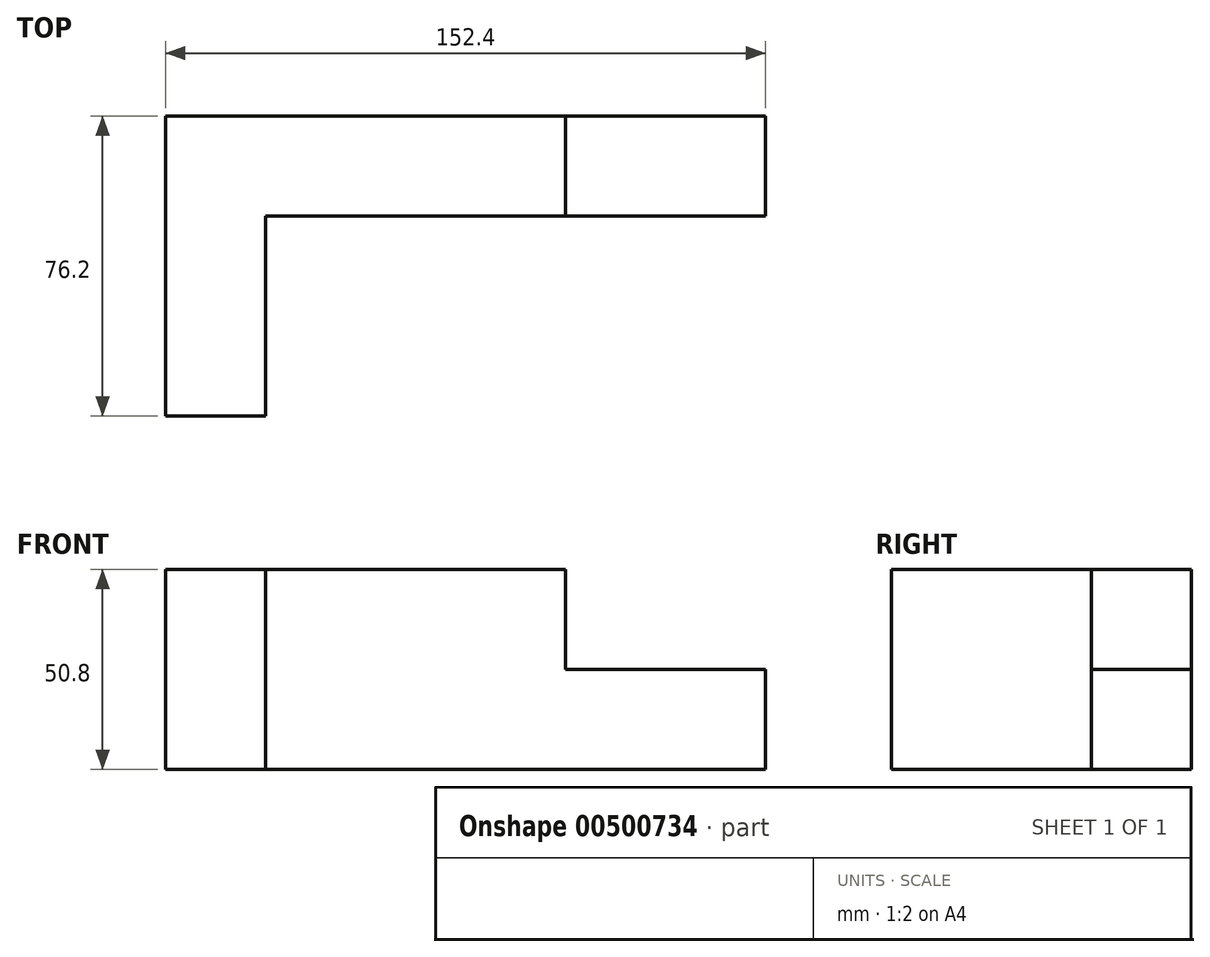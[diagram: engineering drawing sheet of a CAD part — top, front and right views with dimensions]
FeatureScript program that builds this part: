
annotation { "Feature Type Name" : "Feature", "Feature Type Description" : "" }
export const myFeature = defineFeature(function(context is Context, id is Id, definition is map)
    precondition{}
    {
        {
            var Q0;
            Q0=qCreatedBy(makeId("Top.planeOp"),FACE);
            var sketch = newSketch(context, id + "F0", { "sketchPlane" : qUnion([Q0])});
            skLineSegment(sketch, "E0.bottom", {"start": v(-48.05, 62.68) * mm, "end": v(-22.65, 62.68) * mm});
            skLineSegment(sketch, "E0.top", {"start": v(-48.05, -13.52) * mm, "end": v(-22.65, -13.52) * mm});
            skLineSegment(sketch, "E0.left", {"start": v(-48.05, 62.68) * mm, "end": v(-48.05, -13.52) * mm});
            skLineSegment(sketch, "E0.right", {"start": v(-22.65, 62.68) * mm, "end": v(-22.65, -13.52) * mm});
            skLineSegment(sketch, "E1.bottom", {"start": v(-22.65, 62.68) * mm, "end": v(53.55, 62.68) * mm});
            skLineSegment(sketch, "E1.top", {"start": v(-22.65, 37.28) * mm, "end": v(53.55, 37.28) * mm});
            skLineSegment(sketch, "E1.left", {"start": v(-22.65, 62.68) * mm, "end": v(-22.65, 37.28) * mm});
            skLineSegment(sketch, "E1.right", {"start": v(53.55, 62.68) * mm, "end": v(53.55, 37.28) * mm});
            skLineSegment(sketch, "E2.bottom", {"start": v(53.55, 62.68) * mm, "end": v(104.35, 62.68) * mm});
            skLineSegment(sketch, "E2.top", {"start": v(53.55, 37.28) * mm, "end": v(104.35, 37.28) * mm});
            skLineSegment(sketch, "E2.right", {"start": v(104.35, 62.68) * mm, "end": v(104.35, 37.28) * mm});
            skSolve(sketch);
        }
        {
            var Q0;
            Q0=makeQuery(id+"F0.imprint","IMPRINT",FACE,{"disambiguationData":[TD([[makeQuery(id+"F0.imprint","IMPRINT",EDGE,{"derivedFrom":sQuery(id+"F0.wireOp",EDGE,"E0.bottom")}),-1.0]])]});
            extrude(context, id + "F1", {"entities" : qUnion([Q0]), "depth" : 50.8 * mm});
        }
        {
            var Q0;
            Q0=makeQuery(id+"F0.imprint","IMPRINT",FACE,{"disambiguationData":[TD([[makeQuery(id+"F0.imprint","IMPRINT",EDGE,{"derivedFrom":sQuery(id+"F0.wireOp",EDGE,"E1.bottom")}),-1.0]])]});
            extrude(context, id + "F2", {"entities" : qUnion([Q0]), "operationType" : NewBodyOperationType.ADD, "depth" : 50.8 * mm});
        }
        {
            var Q0;
            Q0=makeQuery(id+"F0.imprint","IMPRINT",FACE,{"disambiguationData":[TD([[makeQuery(id+"F0.imprint","IMPRINT",EDGE,{"derivedFrom":sQuery(id+"F0.wireOp",EDGE,"E2.bottom")}),-1.0]])]});
            extrude(context, id + "F3", {"entities" : qUnion([Q0]), "operationType" : NewBodyOperationType.ADD, "depth" : 25.4 * mm});
        }
    });
